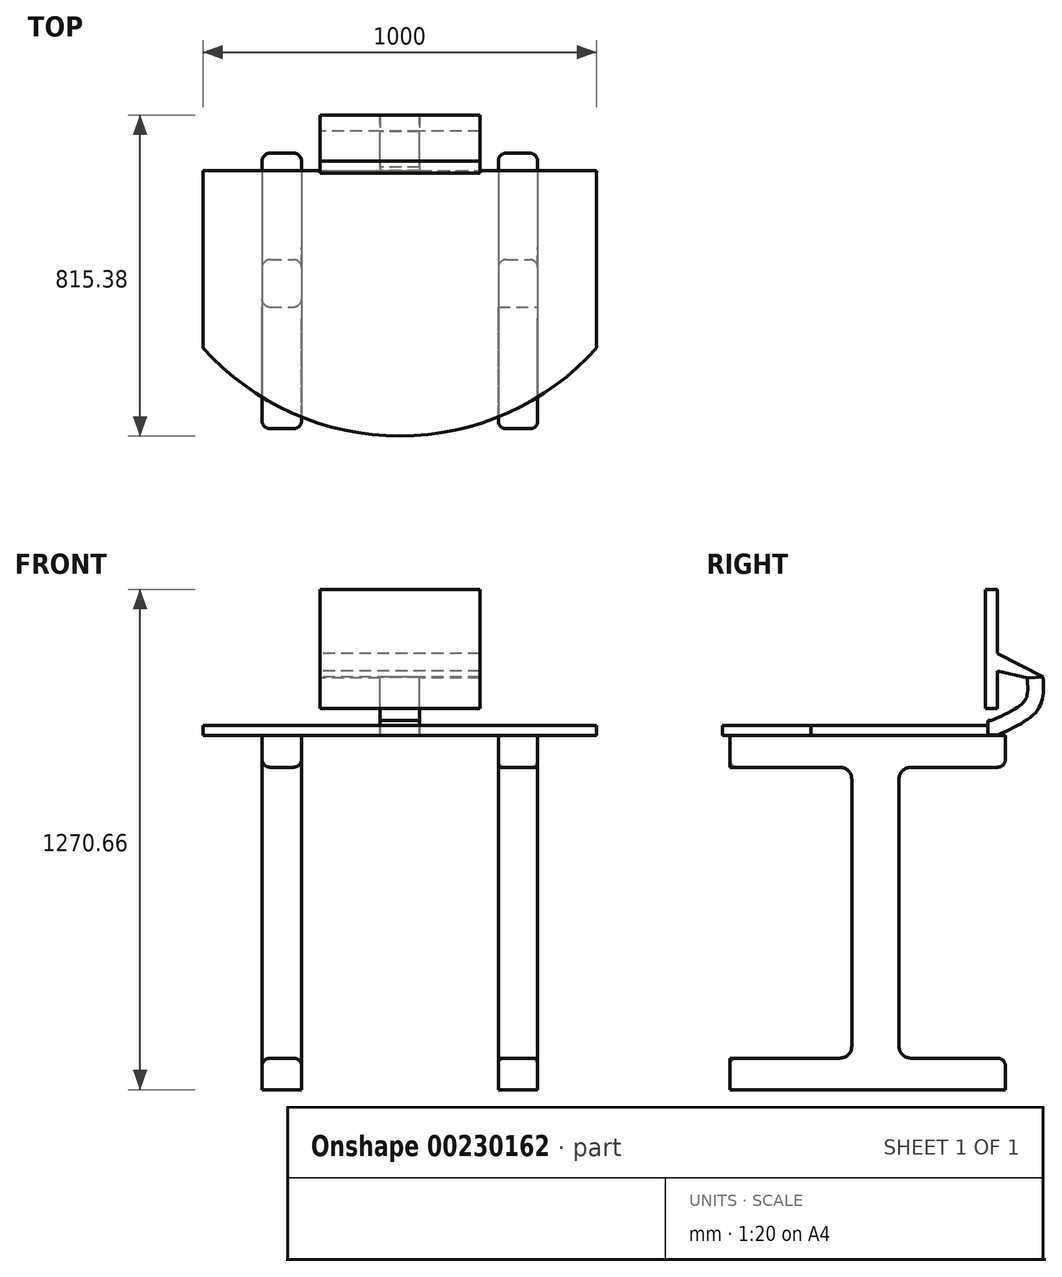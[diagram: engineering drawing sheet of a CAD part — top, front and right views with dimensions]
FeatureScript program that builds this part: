
annotation { "Feature Type Name" : "Feature", "Feature Type Description" : "" }
export const myFeature = defineFeature(function(context is Context, id is Id, definition is map)
    precondition{}
    {
        {
            var Q0;
            Q0=qCreatedBy(makeId("Top.planeOp"),FACE);
            var sketch = newSketch(context, id + "F0", { "sketchPlane" : qUnion([Q0])});
            skLineSegment(sketch, "E0", {"start": v(0, 403.2) * mm, "end": v(0, -299.6) * mm, "construction": true});
            skLineSegment(sketch, "E1.bottom", {"start": v(-330, 398.6) * mm, "end": v(-270, 398.6) * mm});
            skLineSegment(sketch, "E1.top", {"start": v(-330, -301.4) * mm, "end": v(-270, -301.4) * mm});
            skLineSegment(sketch, "E1.left", {"start": v(-350, 378.6) * mm, "end": v(-350, -281.4) * mm});
            skLineSegment(sketch, "E1.right", {"start": v(-250, 378.6) * mm, "end": v(-250, -281.4) * mm});
            skLineSegment(sketch, "E2.MirrorCS", {"start": v(330, -301.4) * mm, "end": v(270, -301.4) * mm});
            skLineSegment(sketch, "E3.MirrorCS", {"start": v(350, 378.6) * mm, "end": v(350, -281.4) * mm});
            skLineSegment(sketch, "E4.MirrorCS", {"start": v(330, 398.6) * mm, "end": v(270, 398.6) * mm});
            skLineSegment(sketch, "E5.MirrorCS", {"start": v(250, 378.6) * mm, "end": v(250, -281.4) * mm});
            skPoint(sketch, "E6.visualSharp", {"position": v(-250, 398.6) * mm});
            skArc(sketch, "E6.filletArc", {"start": v(-250, 378.6) * mm, "mid": v(-255.86, 392.74) * mm, "end": v(-270, 398.6) * mm});
            skPoint(sketch, "E7.visualSharp", {"position": v(-350, 398.6) * mm});
            skArc(sketch, "E7.filletArc", {"start": v(-330, 398.6) * mm, "mid": v(-344.14, 392.74) * mm, "end": v(-350, 378.6) * mm});
            skPoint(sketch, "E8.visualSharp", {"position": v(-350, -301.4) * mm});
            skArc(sketch, "E8.filletArc", {"start": v(-350, -281.4) * mm, "mid": v(-344.14, -295.54) * mm, "end": v(-330, -301.4) * mm});
            skPoint(sketch, "E9.visualSharp", {"position": v(-250, -301.4) * mm});
            skArc(sketch, "E9.filletArc", {"start": v(-270, -301.4) * mm, "mid": v(-255.86, -295.54) * mm, "end": v(-250, -281.4) * mm});
            skPoint(sketch, "E10.visualSharp", {"position": v(250, -301.4) * mm});
            skArc(sketch, "E10.filletArc", {"start": v(250, -281.4) * mm, "mid": v(255.86, -295.54) * mm, "end": v(270, -301.4) * mm});
            skPoint(sketch, "E11.visualSharp", {"position": v(350, -301.4) * mm});
            skArc(sketch, "E11.filletArc", {"start": v(330, -301.4) * mm, "mid": v(344.14, -295.54) * mm, "end": v(350, -281.4) * mm});
            skPoint(sketch, "E12.visualSharp", {"position": v(350, 398.6) * mm});
            skArc(sketch, "E12.filletArc", {"start": v(350, 378.6) * mm, "mid": v(344.14, 392.74) * mm, "end": v(330, 398.6) * mm});
            skPoint(sketch, "E13.visualSharp", {"position": v(250, 398.6) * mm});
            skArc(sketch, "E13.filletArc", {"start": v(270, 398.6) * mm, "mid": v(255.86, 392.74) * mm, "end": v(250, 378.6) * mm});
            skSolve(sketch);
        }
        {
            var Q0;
            Q0=makeQuery(id+"F0.imprint","IMPRINT",FACE,{"disambiguationData":[TD([[makeQuery(id+"F0.imprint","IMPRINT",EDGE,{"derivedFrom":sQuery(id+"F0.wireOp",EDGE,"E2.MirrorCS")}),-1.0]])]});
            var Q1;
            Q1=makeQuery(id+"F0.imprint","IMPRINT",FACE,{"disambiguationData":[TD([[makeQuery(id+"F0.imprint","IMPRINT",EDGE,{"derivedFrom":sQuery(id+"F0.wireOp",EDGE,"E1.bottom")}),-1.0]])]});
            extrude(context, id + "F1", {"entities" : qUnion([Q0, Q1]), "depth" : 900 * mm});
        }
        {
            var Q0;
            Q0=makeQuery(id+"F1.opExtrude","CAP_FACE",FACE,{"disambiguationData":[OSD([sQuery(id+"F0.wireOp",EDGE,"E1.bottom"),sQuery(id+"F0.wireOp",EDGE,"E1.top"),sQuery(id+"F0.wireOp",EDGE,"E1.left"),sQuery(id+"F0.wireOp",EDGE,"E1.right"),sQuery(id+"F0.wireOp",EDGE,"E6.filletArc"),sQuery(id+"F0.wireOp",EDGE,"E7.filletArc"),sQuery(id+"F0.wireOp",EDGE,"E8.filletArc"),sQuery(id+"F0.wireOp",EDGE,"E9.filletArc")])],"isStart":false});
            var sketch = newSketch(context, id + "F2", { "sketchPlane" : qUnion([Q0])});
            skLineSegment(sketch, "E14", {"start": v(0, 0) * mm, "end": v(0, 363.1) * mm, "construction": true});
            skLineSegment(sketch, "E15", {"start": v(0, 354.1) * mm, "end": v(500, 354.1) * mm});
            skLineSegment(sketch, "E16", {"start": v(500, 354.1) * mm, "end": v(500, -95.9) * mm});
            skLineSegment(sketch, "E17.MirrorCS", {"start": v(0, 354.1) * mm, "end": v(-500, 354.1) * mm});
            skLineSegment(sketch, "E18.MirrorCS", {"start": v(-500, 354.1) * mm, "end": v(-500, -95.9) * mm});
            skArc(sketch, "E19", {"start": v(-500, -95.9) * mm, "mid": v(0, -319.97) * mm, "end": v(500, -95.9) * mm});
            skSolve(sketch);
        }
        {
            var Q0;
            Q0 = qSketchRegion(id + "F2", true);
            extrude(context, id + "F3", {"entities" : qUnion([Q0]), "depth" : 25 * mm});
        }
        {
            var Q0;
            Q0=makeQuery(id+"F1.opExtrude","SWEPT_FACE",FACE,{"disambiguationData":[OSD([sQuery(id+"F0.wireOp",EDGE,"E3.MirrorCS")])]});
            var sketch = newSketch(context, id + "F4", { "sketchPlane" : qUnion([Q0])});
            skLineSegment(sketch, "E20.bottom", {"start": v(-362.49, 819.22) * mm, "end": v(-22, 819.22) * mm});
            skLineSegment(sketch, "E20.top", {"start": v(-362.49, 80.05) * mm, "end": v(-22, 80.05) * mm});
            skLineSegment(sketch, "E20.left", {"start": v(-362.49, 819.22) * mm, "end": v(-362.49, 80.05) * mm});
            skLineSegment(sketch, "E20.right", {"start": v(8, 789.22) * mm, "end": v(8, 110.05) * mm});
            skPoint(sketch, "E21.visualSharp", {"position": v(8, 819.22) * mm});
            skArc(sketch, "E21.filletArc", {"start": v(8, 789.22) * mm, "mid": v(-0.78, 810.44) * mm, "end": v(-22, 819.22) * mm});
            skPoint(sketch, "E22.visualSharp", {"position": v(8, 80.05) * mm});
            skArc(sketch, "E22.filletArc", {"start": v(-22, 80.05) * mm, "mid": v(-0.78, 88.84) * mm, "end": v(8, 110.05) * mm});
            skLineSegment(sketch, "E23", {"start": v(68.1, 819.22) * mm, "end": v(68.1, 78.28) * mm});
            skLineSegment(sketch, "E24.MirrorCS", {"start": v(498.7, 819.22) * mm, "end": v(158.2, 819.22) * mm});
            skArc(sketch, "E25.MirrorCS", {"start": v(128.2, 789.22) * mm, "mid": v(137, 810.44) * mm, "end": v(158.2, 819.22) * mm});
            skLineSegment(sketch, "E26.MirrorCS", {"start": v(128.2, 789.22) * mm, "end": v(128.2, 110.05) * mm});
            skArc(sketch, "E27.MirrorCS", {"start": v(158.2, 80.05) * mm, "mid": v(137, 88.84) * mm, "end": v(128.2, 110.05) * mm});
            skLineSegment(sketch, "E28.MirrorCS", {"start": v(498.7, 80.05) * mm, "end": v(158.2, 80.05) * mm});
            skLineSegment(sketch, "E29.MirrorCS", {"start": v(498.7, 819.22) * mm, "end": v(498.7, 80.05) * mm});
            skSolve(sketch);
        }
        {
            var Q0;
            Q0 = qSketchRegion(id + "F4", true);
            extrude(context, id + "F5", {"entities" : qUnion([Q0]), "operationType" : NewBodyOperationType.REMOVE, "oppositeDirection" : true, "depth" : 759 * mm});
        }
        {
            var Q0;
            Q0=qCreatedBy(makeId("Right.planeOp"),FACE);
            var sketch = newSketch(context, id + "F6", { "sketchPlane" : qUnion([Q0])});
            skFitSpline(sketch, "E30", {"points": [v(379.83, 901.13) * mm, v(482.83, 968.67) * mm, v(493.8, 1049.72) * mm], "startDerivative": vector(231.7, 106.62) * mm, "endDerivative": vector(-12.03, 193.52) * mm});
            skFitSpline(sketch, "E31.0", {"points": [v(363.1, 937.46) * mm, v(367.93, 939.69) * mm, v(377.47, 944.07) * mm, v(391.18, 950.55) * mm, v(404.06, 956.98) * mm, v(415.85, 963.35) * mm, v(424.53, 968.6) * mm, v(430.66, 972.72) * mm, v(434.82, 975.74) * mm, v(438.5, 978.68) * mm, v(441.69, 981.49) * mm, v(444.37, 984.13) * mm, v(446.18, 986.17) * mm, v(447.38, 987.68) * mm, v(448.17, 988.75) * mm, v(448.73, 989.6) * mm, v(449.13, 990.22) * mm, v(449.52, 990.87) * mm, v(449.98, 991.7) * mm, v(450.68, 993.07) * mm, v(451.48, 994.93) * mm, v(452.35, 997.44) * mm, v(453.12, 1000.3) * mm, v(453.77, 1003.5) * mm, v(454.47, 1008.27) * mm, v(455, 1015.15) * mm, v(455.04, 1024.72) * mm, v(454.61, 1035.42) * mm, v(454.13, 1043.2) * mm, v(453.88, 1047.23) * mm]});
            skLineSegment(sketch, "E32", {"start": v(453.88, 1047.23) * mm, "end": v(493.8, 1049.72) * mm});
            skLineSegment(sketch, "E33", {"start": v(363.1, 937.46) * mm, "end": v(353.66, 937.46) * mm});
            skLineSegment(sketch, "E34", {"start": v(379.83, 901.13) * mm, "end": v(353.66, 901.13) * mm});
            skLineSegment(sketch, "E35", {"start": v(353.66, 901.13) * mm, "end": v(353.66, 937.46) * mm});
            skSolve(sketch);
        }
        {
            var Q0;
            Q0 = qSketchRegion(id + "F6", true);
            extrude(context, id + "F7", {"entities" : qUnion([Q0]), "operationType" : NewBodyOperationType.ADD, "depth" : 100 * mm, "symmetric" : true});
        }
        {
            var Q0;
            Q0=qCreatedBy(makeId("Right.planeOp"),FACE);
            var sketch = newSketch(context, id + "F8", { "sketchPlane" : qUnion([Q0])});
            skLineSegment(sketch, "E36.bottom", {"start": v(378.58, 968.52) * mm, "end": v(347.7, 968.52) * mm});
            skLineSegment(sketch, "E36.top", {"start": v(378.58, 1270.66) * mm, "end": v(347.7, 1270.66) * mm});
            skLineSegment(sketch, "E36.left", {"start": v(378.58, 968.52) * mm, "end": v(378.58, 1270.66) * mm});
            skLineSegment(sketch, "E36.right", {"start": v(347.7, 968.52) * mm, "end": v(347.7, 1270.66) * mm});
            skLineSegment(sketch, "E37", {"start": v(378.58, 1063.86) * mm, "end": v(455.12, 1046.4) * mm});
            skLineSegment(sketch, "E38", {"start": v(495.41, 1049.09) * mm, "end": v(378.58, 1108.18) * mm});
            skLineSegment(sketch, "E39", {"start": v(455.12, 1046.4) * mm, "end": v(495.41, 1049.09) * mm});
            skSolve(sketch);
        }
        {
            var Q0;
            Q0 = qSketchRegion(id + "F8", true);
            extrude(context, id + "F9", {"entities" : qUnion([Q0]), "operationType" : NewBodyOperationType.ADD, "depth" : 406 * mm, "symmetric" : true});
        }
        {
            var Q0;
            Q0=makeQuery(id+"F5.boolean.opBoolean","COPY",EDGE,{"derivedFrom":makeQuery(id+"F5.opExtrude","CAP_EDGE",EDGE,{"disambiguationData":[OSD([sQuery(id+"F4.wireOp",EDGE,"E20.top")])],"isStart":true})});
            var Q1;
            Q1=makeQuery(id+"F5.boolean.opBoolean","INTERSECT",EDGE,{"derivedFrom":[makeQuery(id+"F1.opExtrude","SWEPT_FACE",FACE,{"disambiguationData":[OSD([sQuery(id+"F0.wireOp",EDGE,"E1.right")])]}),makeQuery(id+"F5.opExtrude","SWEPT_FACE",FACE,{"disambiguationData":[OSD([sQuery(id+"F4.wireOp",EDGE,"E20.top")])]})]});
            var Q2;
            Q2=makeQuery(id+"F5.boolean.opBoolean","INTERSECT",EDGE,{"derivedFrom":[makeQuery(id+"F1.opExtrude","SWEPT_FACE",FACE,{"disambiguationData":[OSD([sQuery(id+"F0.wireOp",EDGE,"E1.left")])]}),makeQuery(id+"F5.opExtrude","SWEPT_FACE",FACE,{"disambiguationData":[OSD([sQuery(id+"F4.wireOp",EDGE,"E28.MirrorCS")])]})]});
            var Q3;
            Q3=makeQuery(id+"F5.boolean.opBoolean","INTERSECT",EDGE,{"derivedFrom":[makeQuery(id+"F1.opExtrude","SWEPT_FACE",FACE,{"disambiguationData":[OSD([sQuery(id+"F0.wireOp",EDGE,"E5.MirrorCS")])]}),makeQuery(id+"F5.opExtrude","SWEPT_FACE",FACE,{"disambiguationData":[OSD([sQuery(id+"F4.wireOp",EDGE,"E28.MirrorCS")])]})]});
            fillet(context, id + "F10", {"entities" : qUnion([Q0, Q1, Q2, Q3]), "radius" : 20 * mm, "tangentPropagation" : true, "allowEdgeOverflow" : false});
        }
    });
